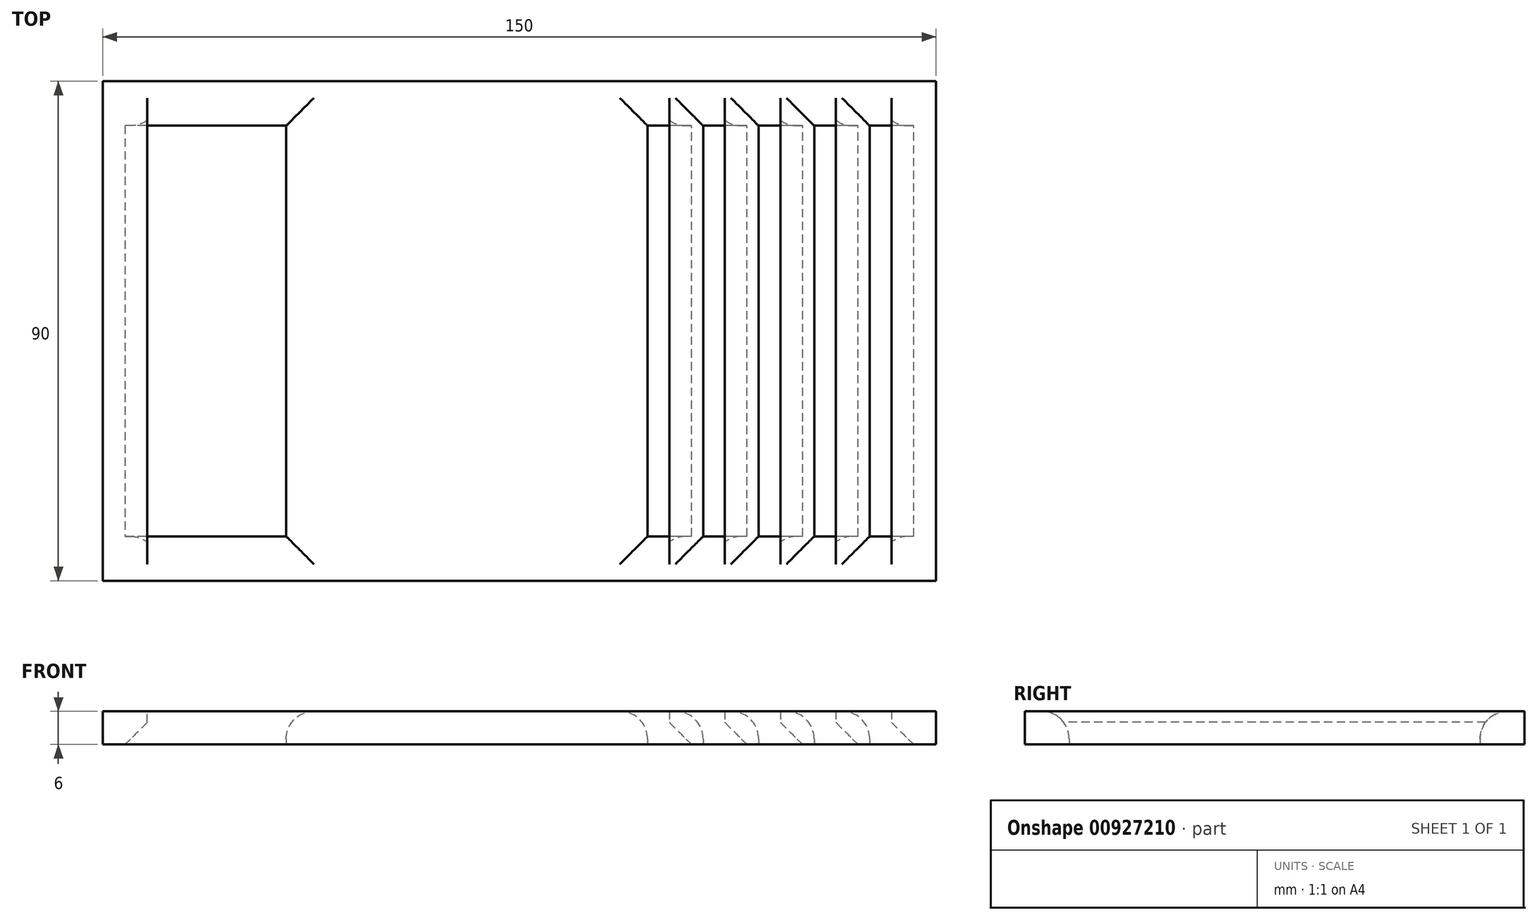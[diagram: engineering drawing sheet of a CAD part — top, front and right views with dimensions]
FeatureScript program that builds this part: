
annotation { "Feature Type Name" : "Feature", "Feature Type Description" : "" }
export const myFeature = defineFeature(function(context is Context, id is Id, definition is map)
    precondition{}
    {
        {
            var Q0;
            Q0=qCreatedBy(makeId("Top.planeOp"),FACE);
            var sketch = newSketch(context, id + "F0", { "sketchPlane" : qUnion([Q0])});
            skLineSegment(sketch, "E0.bottom", {"start": v(75, 45) * mm, "end": v(-75, 45) * mm});
            skLineSegment(sketch, "E0.top", {"start": v(75, -45) * mm, "end": v(-75, -45) * mm});
            skLineSegment(sketch, "E0.left", {"start": v(75, 45) * mm, "end": v(75, -45) * mm});
            skLineSegment(sketch, "E0.right", {"start": v(-75, 45) * mm, "end": v(-75, -45) * mm});
            skPoint(sketch, "E0.middle", {"position": v(0, 0) * mm});
            skLineSegment(sketch, "E1.0", {"start": v(67, 37) * mm, "end": v(63.09, 37) * mm});
            skLineSegment(sketch, "E1.1", {"start": v(67, 37) * mm, "end": v(67, -37) * mm});
            skLineSegment(sketch, "E1.2", {"start": v(67, -37) * mm, "end": v(63.09, -37) * mm});
            skLineSegment(sketch, "E1.3", {"start": v(-67, 37) * mm, "end": v(-67, -37) * mm});
            skLineSegment(sketch, "E2", {"start": v(-67, 22.63) * mm, "end": v(-42, 22.63) * mm, "construction": true});
            skLineSegment(sketch, "E3", {"start": v(-42, 37) * mm, "end": v(-42, -37) * mm});
            skLineSegment(sketch, "E4", {"start": v(67, 30.97) * mm, "end": v(63, 30.97) * mm, "construction": true});
            skLineSegment(sketch, "E5", {"start": v(63.09, 37) * mm, "end": v(63.09, -37) * mm});
            skLineSegment(sketch, "E6.1.0.0", {"start": v(57, 37) * mm, "end": v(57, -37) * mm});
            skLineSegment(sketch, "E6.1.0.1", {"start": v(53.09, 37) * mm, "end": v(53.09, -37) * mm});
            skLineSegment(sketch, "E6.2.0.0", {"start": v(47, 37) * mm, "end": v(47, -37) * mm});
            skLineSegment(sketch, "E6.2.0.1", {"start": v(43.09, 37) * mm, "end": v(43.09, -37) * mm});
            skLineSegment(sketch, "E6.3.0.0", {"start": v(37, 37) * mm, "end": v(37, -37) * mm});
            skLineSegment(sketch, "E6.3.0.1", {"start": v(33.09, 37) * mm, "end": v(33.09, -37) * mm});
            skLineSegment(sketch, "E6.4.0.0", {"start": v(27, 37) * mm, "end": v(27, -37) * mm});
            skLineSegment(sketch, "E6.4.0.1", {"start": v(23.09, 37) * mm, "end": v(23.09, -37) * mm});
            skLineSegment(sketch, "E6.direction1", {"start": v(67, -37) * mm, "end": v(63.09, -37) * mm, "construction": true});
            skLineSegment(sketch, "E7.trimOffspring", {"start": v(57, 37) * mm, "end": v(53.09, 37) * mm});
            skLineSegment(sketch, "E8.trimOffspring", {"start": v(47, 37) * mm, "end": v(43.09, 37) * mm});
            skLineSegment(sketch, "E9.trimOffspring", {"start": v(37, 37) * mm, "end": v(33.09, 37) * mm});
            skLineSegment(sketch, "E10.trimOffspring", {"start": v(27, 37) * mm, "end": v(23.09, 37) * mm});
            skLineSegment(sketch, "E11.trimOffspring", {"start": v(-42, 37) * mm, "end": v(-67, 37) * mm});
            skLineSegment(sketch, "E12.trimOffspring", {"start": v(57, -37) * mm, "end": v(53.09, -37) * mm});
            skLineSegment(sketch, "E13.trimOffspring", {"start": v(47, -37) * mm, "end": v(43.09, -37) * mm});
            skLineSegment(sketch, "E14.trimOffspring", {"start": v(37, -37) * mm, "end": v(33.09, -37) * mm});
            skLineSegment(sketch, "E15.trimOffspring", {"start": v(27, -37) * mm, "end": v(23.09, -37) * mm});
            skLineSegment(sketch, "E16.trimOffspring", {"start": v(-42, -37) * mm, "end": v(-67, -37) * mm});
            skSolve(sketch);
        }
        {
            var Q0;
            Q0=makeQuery(id+"F0.imprint","IMPRINT",FACE,{"disambiguationData":[TD([[makeQuery(id+"F0.imprint","IMPRINT",EDGE,{"derivedFrom":sQuery(id+"F0.wireOp",EDGE,"E0.bottom")}),1.0]])]});
            extrude(context, id + "F1", {"entities" : qUnion([Q0]), "depth" : 6 * mm, "offsetDistance" : 25 * mm});
        }
        {
            var Q0;
            Q0=makeQuery(id+"F1.opExtrude","CAP_EDGE",EDGE,{"disambiguationData":[OSD([sQuery(id+"F0.wireOp",EDGE,"E11.trimOffspring")])],"isStart":false});
            var Q1;
            Q1=makeQuery(id+"F1.opExtrude","CAP_EDGE",EDGE,{"disambiguationData":[OSD([sQuery(id+"F0.wireOp",EDGE,"E3")])],"isStart":false});
            var Q2;
            Q2=makeQuery(id+"F1.opExtrude","CAP_EDGE",EDGE,{"disambiguationData":[OSD([sQuery(id+"F0.wireOp",EDGE,"E16.trimOffspring")])],"isStart":false});
            var Q3;
            Q3=makeQuery(id+"F1.opExtrude","CAP_EDGE",EDGE,{"disambiguationData":[OSD([sQuery(id+"F0.wireOp",EDGE,"E6.4.0.1")])],"isStart":false});
            var Q4;
            Q4=makeQuery(id+"F1.opExtrude","CAP_EDGE",EDGE,{"disambiguationData":[OSD([sQuery(id+"F0.wireOp",EDGE,"E6.3.0.1")])],"isStart":false});
            var Q5;
            Q5=makeQuery(id+"F1.opExtrude","CAP_EDGE",EDGE,{"disambiguationData":[OSD([sQuery(id+"F0.wireOp",EDGE,"E6.2.0.1")])],"isStart":false});
            var Q6;
            Q6=makeQuery(id+"F1.opExtrude","CAP_EDGE",EDGE,{"disambiguationData":[OSD([sQuery(id+"F0.wireOp",EDGE,"E6.1.0.1")])],"isStart":false});
            var Q7;
            Q7=makeQuery(id+"F1.opExtrude","CAP_EDGE",EDGE,{"disambiguationData":[OSD([sQuery(id+"F0.wireOp",EDGE,"E5")])],"isStart":false});
            var Q8;
            Q8=makeQuery(id+"F1.opExtrude","CAP_EDGE",EDGE,{"disambiguationData":[OSD([sQuery(id+"F0.wireOp",EDGE,"E10.trimOffspring")])],"isStart":false});
            var Q9;
            Q9=makeQuery(id+"F1.opExtrude","CAP_EDGE",EDGE,{"disambiguationData":[OSD([sQuery(id+"F0.wireOp",EDGE,"E9.trimOffspring")])],"isStart":false});
            var Q10;
            Q10=makeQuery(id+"F1.opExtrude","CAP_EDGE",EDGE,{"disambiguationData":[OSD([sQuery(id+"F0.wireOp",EDGE,"E8.trimOffspring")])],"isStart":false});
            var Q11;
            Q11=makeQuery(id+"F1.opExtrude","CAP_EDGE",EDGE,{"disambiguationData":[OSD([sQuery(id+"F0.wireOp",EDGE,"E7.trimOffspring")])],"isStart":false});
            var Q12;
            Q12=makeQuery(id+"F1.opExtrude","CAP_EDGE",EDGE,{"disambiguationData":[OSD([sQuery(id+"F0.wireOp",EDGE,"E1.0")])],"isStart":false});
            var Q13;
            Q13=makeQuery(id+"F1.opExtrude","CAP_EDGE",EDGE,{"disambiguationData":[OSD([sQuery(id+"F0.wireOp",EDGE,"E1.2")])],"isStart":false});
            var Q14;
            Q14=makeQuery(id+"F1.opExtrude","CAP_EDGE",EDGE,{"disambiguationData":[OSD([sQuery(id+"F0.wireOp",EDGE,"E12.trimOffspring")])],"isStart":false});
            var Q15;
            Q15=makeQuery(id+"F1.opExtrude","CAP_EDGE",EDGE,{"disambiguationData":[OSD([sQuery(id+"F0.wireOp",EDGE,"E13.trimOffspring")])],"isStart":false});
            var Q16;
            Q16=makeQuery(id+"F1.opExtrude","CAP_EDGE",EDGE,{"disambiguationData":[OSD([sQuery(id+"F0.wireOp",EDGE,"E14.trimOffspring")])],"isStart":false});
            var Q17;
            Q17=makeQuery(id+"F1.opExtrude","CAP_EDGE",EDGE,{"disambiguationData":[OSD([sQuery(id+"F0.wireOp",EDGE,"E15.trimOffspring")])],"isStart":false});
            fillet(context, id + "F2", {"entities" : qUnion([Q0, Q1, Q2, Q3, Q4, Q5, Q6, Q7, Q8, Q9, Q10, Q11, Q12, Q13, Q14, Q15, Q16, Q17]), "radius" : 5 * mm, "tangentPropagation" : true, "allowEdgeOverflow" : false});
        }
        {
            var Q0;
            Q0=makeQuery(id+"F1.opExtrude","CAP_EDGE",EDGE,{"disambiguationData":[OSD([sQuery(id+"F0.wireOp",EDGE,"E1.3")])],"isStart":true});
            var Q1;
            Q1=makeQuery(id+"F1.opExtrude","CAP_EDGE",EDGE,{"disambiguationData":[OSD([sQuery(id+"F0.wireOp",EDGE,"E6.4.0.0")])],"isStart":true});
            var Q2;
            Q2=makeQuery(id+"F1.opExtrude","CAP_EDGE",EDGE,{"disambiguationData":[OSD([sQuery(id+"F0.wireOp",EDGE,"E6.3.0.0")])],"isStart":true});
            var Q3;
            Q3=makeQuery(id+"F1.opExtrude","CAP_EDGE",EDGE,{"disambiguationData":[OSD([sQuery(id+"F0.wireOp",EDGE,"E6.2.0.0")])],"isStart":true});
            var Q4;
            Q4=makeQuery(id+"F1.opExtrude","CAP_EDGE",EDGE,{"disambiguationData":[OSD([sQuery(id+"F0.wireOp",EDGE,"E6.1.0.0")])],"isStart":true});
            var Q5;
            Q5=makeQuery(id+"F1.opExtrude","CAP_EDGE",EDGE,{"disambiguationData":[OSD([sQuery(id+"F0.wireOp",EDGE,"E1.1")])],"isStart":true});
            chamfer(context, id + "F3", {"entities" : qUnion([Q0, Q1, Q2, Q3, Q4, Q5]), "width" : 4 * mm, "tangentPropagation" : true});
        }
    });
